# Revit family: LSER24
name_source: partatom
category: Lighting Fixtures
revit_build: Autodesk Revit MEP 2012 (Build: 20110309_2315(x64)
units: mm (PartAtom-declared; Revit-internal decimal feet)

## types (24) — shared parameters
Apparent Load = 0 VA
Color Filter = 16777215
Default Elevation = 4' - 0"
Dimming Lamp Color Temperature Shift = <None>
IES FILE LINK = http://www.columbialighting.com
LEGNTH = 4' - 6"
Manufacturer = COLUMBIA
Model = LSER22
Number of Poles = 1
Power Factor = 1
Product Documentation Link = http://www.columbialighting.com
Product Page URL = http://www.columbialighting.com
Tilt Angle = 90.00°
Voltage = 0 V
WIDTH = 2' - 0"

## per-type parameters (varying)
| type | Photometric Web File | Wattage Comments |
| LSER24-40VLG-R-ESD | itl78386.ies |  |
| LSER24-40VLG-C-ESD | itl78384.ies |  |
| LSER24-40MLG-R-ESD | itl78378.ies |  |
| LSER24-40MLG-C-ESD | itl78375.ies |  |
| LSER24-40LWG-R-ESD | itl78462.ies |  |
| LSER24-40LWG-C-ESD | itl78459.ies |  |
| LSER24-40HLG-R-ESD | itl78382.ies |  |
| LSER24-40HLG-C-ESD | itl78380.ies |  |
| LSER24-35VLG-R-ESD | itl78385.ies |  |
| LSER24-35VLG-C-ESD | itl78383.ies |  |
| LSER24-35MLG-R-ESD | itl78377.ies |  |
| LSER24-35MLG-C-ESD | itl78374.ies |  |
| LSER24-35LWG-R-ESD | itl78461.ies |  |
| LSER24-35LWG-C-ESD | itl78458.ies |  |
| LSER24-35HLG-R-ESD | itl78381.ies |  |
| LSER24-35HLG-C-ESD | itl78379.ies |  |
| LSER24-30VLG-R-ESD | itl78390.ies |  |
| LSER24-30VLG-C-ESD | itl78389.ies |  |
| LSER24-30MLG-R-ESD | itl78376.ies |  |
| LSER24-30MLG-C-ESD | itl78373.ies |  |
| LSER24-30LWG-R-ESD | itl78460.ies |  |
| LSER24-30LWG-C-ESD | itl78457.ies |  |
| LSER24-30HLG-R-ESD | itl78388.ies | 61.6 |
| LSER24-30HLG-C-ESD | itl78387.ies | 61.6 |

## geometry (parser evidence)
native form markers: Sweep x2
no freeform markers — native parametric forms only
